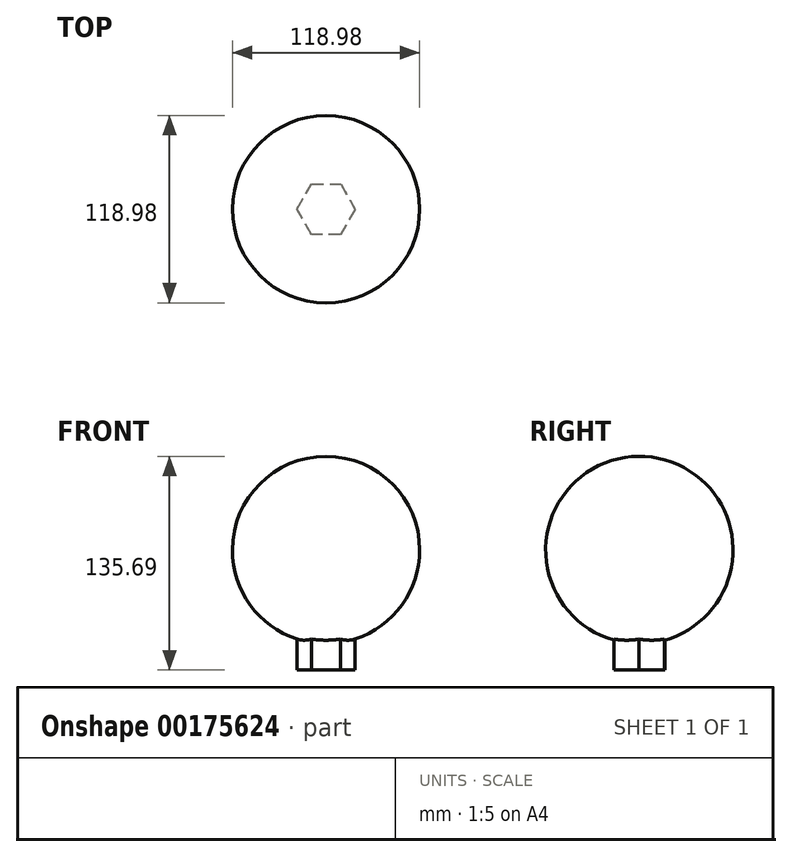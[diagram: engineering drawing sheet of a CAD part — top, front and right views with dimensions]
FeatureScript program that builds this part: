
annotation { "Feature Type Name" : "Feature", "Feature Type Description" : "" }
export const myFeature = defineFeature(function(context is Context, id is Id, definition is map)
    precondition{}
    {
        {
            var Q0;
            Q0=qCreatedBy(makeId("Top.planeOp"),FACE);
            var sketch = newSketch(context, id + "F0", { "sketchPlane" : qUnion([Q0])});
            skArc(sketch, "E0", {"start": v(59.49, 0) * mm, "mid": v(0, 59.49) * mm, "end": v(-59.49, 0) * mm});
            skLineSegment(sketch, "E1", {"start": v(-59.49, 0) * mm, "end": v(59.49, 0) * mm});
            skSolve(sketch);
        }
        {
            var Q0;
            Q0 = qSketchRegion(id + "F0", true);
            var Q1;
            Q1=sQuery(id+"F0.wireOp",EDGE,"E1");
            revolve(context, id + "F1", {"entities" : qUnion([Q0]), "axis" : qUnion([Q1]), "revolveType" : RevolveType.FULL});
        }
        {
            var Q0;
            Q0=qCreatedBy(makeId("Top.planeOp"),FACE);
            var sketch = newSketch(context, id + "F2", { "sketchPlane" : qUnion([Q0])});
            skCircle(sketch, "E2.cCircle", {"center": v(0, 0) * mm, "radius": 18.52 * mm, "construction": true});
            skLineSegment(sketch, "E2.0", {"start": v(-9.13, 16.12) * mm, "end": v(9.4, 15.96) * mm});
            skLineSegment(sketch, "E2.1", {"start": v(9.4, 15.96) * mm, "end": v(18.52, -0.15) * mm});
            skLineSegment(sketch, "E2.2", {"start": v(18.52, -0.15) * mm, "end": v(9.13, -16.12) * mm});
            skLineSegment(sketch, "E2.3", {"start": v(9.13, -16.12) * mm, "end": v(-9.4, -15.96) * mm});
            skLineSegment(sketch, "E2.4", {"start": v(-9.4, -15.96) * mm, "end": v(-18.52, 0.15) * mm});
            skLineSegment(sketch, "E2.5", {"start": v(-18.52, 0.15) * mm, "end": v(-9.13, 16.12) * mm});
            skSolve(sketch);
        }
        {
            var Q0;
            Q0 = qSketchRegion(id + "F2", true);
            extrude(context, id + "F3", {"entities" : qUnion([Q0]), "operationType" : NewBodyOperationType.ADD, "oppositeDirection" : true, "depth" : 76.2 * mm});
        }
    });
